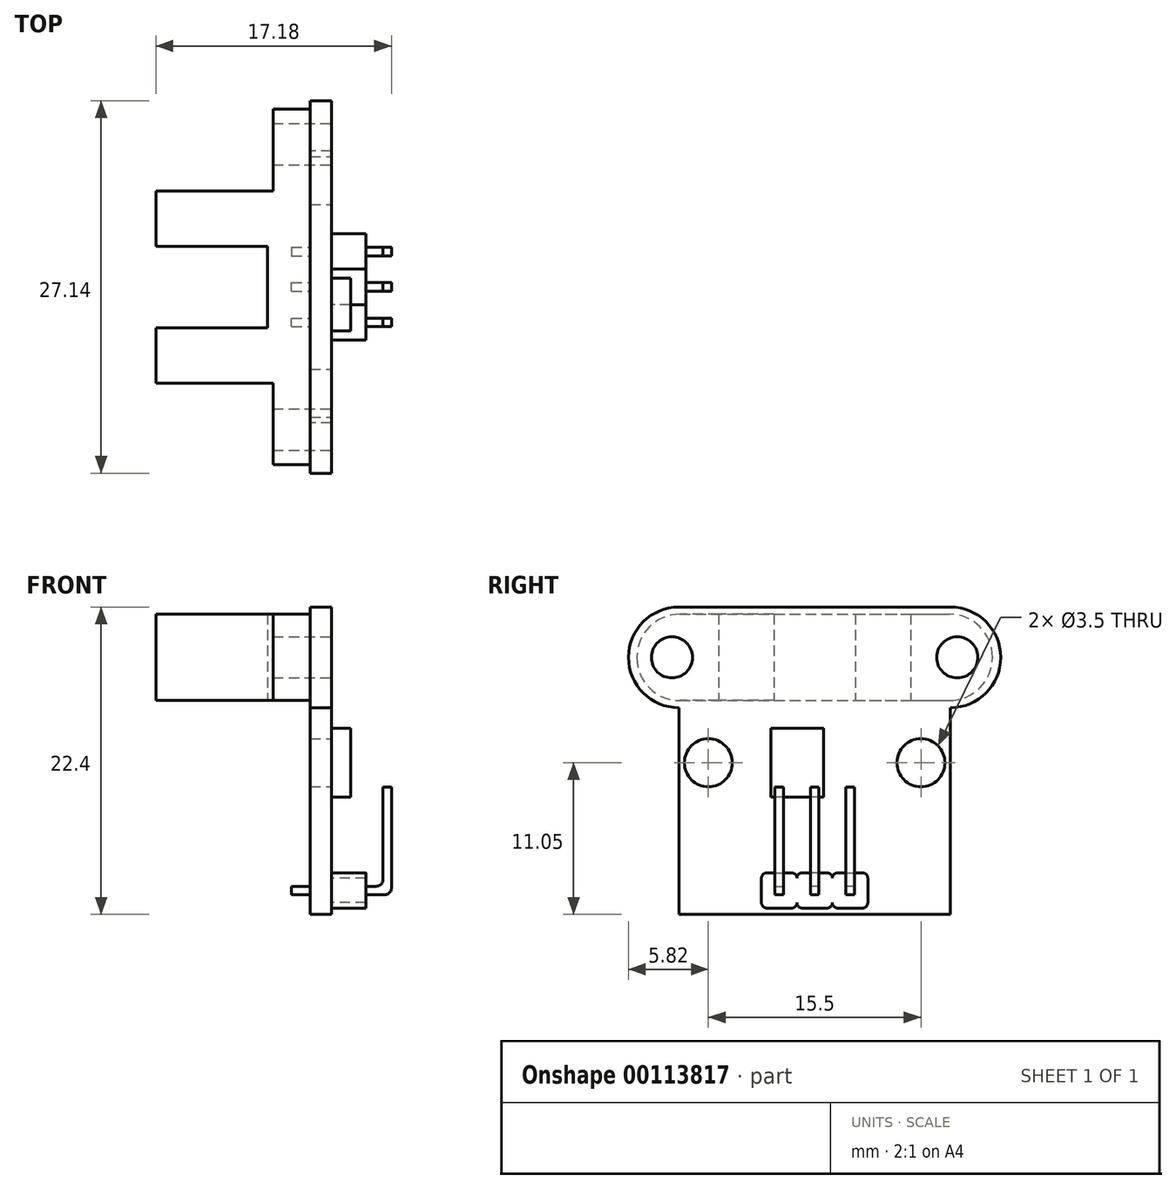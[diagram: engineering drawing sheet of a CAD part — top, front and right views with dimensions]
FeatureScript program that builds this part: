
annotation { "Feature Type Name" : "Feature", "Feature Type Description" : "" }
export const myFeature = defineFeature(function(context is Context, id is Id, definition is map)
    precondition{}
    {
        {
            var Q0;
            Q0=qCreatedBy(makeId("Top.planeOp"),FACE);
            var sketch = newSketch(context, id + "F0", { "sketchPlane" : qUnion([Q0])});
            skLineSegment(sketch, "E0", {"start": v(0, 0) * mm, "end": v(83.87, 0) * mm, "construction": true});
            skLineSegment(sketch, "E1", {"start": v(0, 0) * mm, "end": v(0, -2.97) * mm});
            skLineSegment(sketch, "E2", {"start": v(0, -2.97) * mm, "end": v(-8.13, -2.97) * mm});
            skLineSegment(sketch, "E3", {"start": v(-8.13, -2.97) * mm, "end": v(-8.13, -7) * mm});
            skLineSegment(sketch, "E4", {"start": v(-8.13, -7) * mm, "end": v(0.41, -7) * mm});
            skLineSegment(sketch, "E5", {"start": v(0.41, -7) * mm, "end": v(0.41, -12.97) * mm});
            skLineSegment(sketch, "E6", {"start": v(0.41, -12.96) * mm, "end": v(3.13, -12.96) * mm});
            skLineSegment(sketch, "E7", {"start": v(3.13, -12.96) * mm, "end": v(3.13, 0) * mm});
            skLineSegment(sketch, "E8.MirrorCS", {"start": v(0.41, 7) * mm, "end": v(0.41, 12.97) * mm});
            skLineSegment(sketch, "E9.MirrorCS", {"start": v(0.4, 12.97) * mm, "end": v(3.13, 12.97) * mm});
            skLineSegment(sketch, "E10.MirrorCS", {"start": v(0, 0) * mm, "end": v(0, 2.97) * mm});
            skLineSegment(sketch, "E11.MirrorCS", {"start": v(3.13, 12.96) * mm, "end": v(3.13, 0) * mm});
            skLineSegment(sketch, "E12.MirrorCS", {"start": v(0, 2.97) * mm, "end": v(-8.13, 2.97) * mm});
            skLineSegment(sketch, "E13.MirrorCS", {"start": v(-8.13, 7) * mm, "end": v(0.41, 7) * mm});
            skLineSegment(sketch, "E14.MirrorCS", {"start": v(-8.13, 2.97) * mm, "end": v(-8.13, 7) * mm});
            skLineSegment(sketch, "E15", {"start": v(-8.13, -2.97) * mm, "end": v(-8.13, 2.97) * mm, "construction": true});
            skSolve(sketch);
        }
        {
            var Q0;
            Q0=qSketchRegion(id+"F0",true);
            extrude(context, id + "F1", {"entities" : qUnion([Q0]), "endBound" : BoundingType.SYMMETRIC, "depth" : 6.3 * mm});
        }
        {
            var Q0;
            Q0=makeQuery(id+"F1.opExtrude","CAP_EDGE",EDGE,{"disambiguationData":[OSD([sQuery(id+"F0.wireOp",EDGE,"E9.MirrorCS")])],"isStart":false});
            var Q1;
            Q1=makeQuery(id+"F1.opExtrude","CAP_EDGE",EDGE,{"disambiguationData":[OSD([sQuery(id+"F0.wireOp",EDGE,"E9.MirrorCS")])],"isStart":true});
            var Q2;
            Q2=makeQuery(id+"F1.opExtrude","CAP_EDGE",EDGE,{"disambiguationData":[OSD([sQuery(id+"F0.wireOp",EDGE,"E6")])],"isStart":false});
            var Q3;
            Q3=makeQuery(id+"F1.opExtrude","CAP_EDGE",EDGE,{"disambiguationData":[OSD([sQuery(id+"F0.wireOp",EDGE,"E6")])],"isStart":true});
            fillet(context, id + "F2", {"entities" : qUnion([Q0, Q1, Q2, Q3]), "radius" : 3.14 * mm, "tangentPropagation" : true, "allowEdgeOverflow" : false});
        }
        {
            var Q0;
            Q0=makeQuery(id+"F1.opExtrude","SWEPT_FACE",FACE,{"disambiguationData":[OSD([sQuery(id+"F0.wireOp",EDGE,"E7"),sQuery(id+"F0.wireOp",EDGE,"E11.MirrorCS")])]});
            var sketch = newSketch(context, id + "F3", { "sketchPlane" : qUnion([Q0])});
            skLineSegment(sketch, "E16", {"start": v(0, 3.15) * mm, "end": v(0, -3.15) * mm, "construction": true});
            skLineSegment(sketch, "E17", {"start": v(-9.9, -18.73) * mm, "end": v(-9.9, -3.67) * mm});
            skArc(sketch, "E18", {"start": v(-9.9, 3.67) * mm, "mid": v(-13.57, 0) * mm, "end": v(-9.9, -3.67) * mm});
            skLineSegment(sketch, "E19.MirrorCS", {"start": v(9.9, -18.73) * mm, "end": v(9.9, -3.67) * mm});
            skArc(sketch, "E20.MirrorCS", {"start": v(9.9, 3.67) * mm, "mid": v(13.57, 0) * mm, "end": v(9.9, -3.67) * mm});
            skLineSegment(sketch, "E21", {"start": v(9.9, 3.67) * mm, "end": v(-9.9, 3.67) * mm});
            skLineSegment(sketch, "E22", {"start": v(9.9, -18.73) * mm, "end": v(-9.9, -18.73) * mm});
            skCircle(sketch, "E23", {"center": v(-9.9, 0) * mm, "radius": 3.67 * mm});
            skCircle(sketch, "E24", {"center": v(9.9, 0) * mm, "radius": 3.67 * mm});
            skSolve(sketch);
        }
        {
            var Q0;
            Q0=makeQuery(id+"F1.opExtrude","SWEPT_FACE",FACE,{"disambiguationData":[OSD([sQuery(id+"F0.wireOp",EDGE,"E7"),sQuery(id+"F0.wireOp",EDGE,"E11.MirrorCS")])]});
            var sketch = newSketch(context, id + "F4", { "sketchPlane" : qUnion([Q0])});
            skLineSegment(sketch, "E25", {"start": v(-9.9, 0) * mm, "end": v(9.9, 0) * mm, "construction": true});
            skCircle(sketch, "E26", {"center": v(-10.4, 0) * mm, "radius": 1.5 * mm});
            skCircle(sketch, "E27.MirrorC", {"center": v(10.4, 0) * mm, "radius": 1.5 * mm});
            skCircle(sketch, "E28", {"center": v(-7.75, -7.68) * mm, "radius": 1.75 * mm});
            skCircle(sketch, "E29.MirrorC", {"center": v(7.75, -7.68) * mm, "radius": 1.75 * mm});
            skSolve(sketch);
        }
        {
            var Q0;
            Q0=qSketchRegion(id+"F3",true);
            extrude(context, id + "F5", {"entities" : qUnion([Q0]), "operationType" : NewBodyOperationType.ADD, "depth" : 1.54 * mm});
        }
        {
            var Q0;
            Q0=qSketchRegion(id+"F4",true);
            extrude(context, id + "F6", {"entities" : qUnion([Q0]), "operationType" : NewBodyOperationType.REMOVE, "endBound" : BoundingType.SYMMETRIC, "oppositeDirection" : true, "depth" : 25 * mm});
        }
        {
            var Q0;
            Q0=makeQuery(id+"F5.opExtrude","CAP_FACE",FACE,{"disambiguationData":[OSD([sQuery(id+"F3.wireOp",EDGE,"E17"),sQuery(id+"F3.wireOp",EDGE,"E18"),sQuery(id+"F3.wireOp",EDGE,"E19.MirrorCS"),sQuery(id+"F3.wireOp",EDGE,"E20.MirrorCS"),sQuery(id+"F3.wireOp",EDGE,"E21"),sQuery(id+"F3.wireOp",EDGE,"E22")])],"isStart":false});
            var sketch = newSketch(context, id + "F7", { "sketchPlane" : qUnion([Q0])});
            skLineSegment(sketch, "E30.bottom", {"start": v(0.9, -15.7) * mm, "end": v(-0.9, -15.7) * mm});
            skLineSegment(sketch, "E30.top", {"start": v(0.9, -18.28) * mm, "end": v(-0.9, -18.28) * mm});
            skLineSegment(sketch, "E30.left", {"start": v(1.3, -16.1) * mm, "end": v(1.3, -17.88) * mm});
            skLineSegment(sketch, "E30.right", {"start": v(-1.3, -16.1) * mm, "end": v(-1.3, -17.88) * mm});
            skPoint(sketch, "E30.middle", {"position": v(0, -16.99) * mm});
            skPoint(sketch, "E31.visualSharp", {"position": v(1.3, -15.7) * mm});
            skArc(sketch, "E31.filletArc", {"start": v(1.3, -16.1) * mm, "mid": v(1.17, -15.81) * mm, "end": v(0.9, -15.7) * mm});
            skPoint(sketch, "E32.visualSharp", {"position": v(1.3, -18.28) * mm});
            skArc(sketch, "E32.filletArc", {"start": v(0.9, -18.28) * mm, "mid": v(1.17, -18.16) * mm, "end": v(1.3, -17.88) * mm});
            skPoint(sketch, "E33.visualSharp", {"position": v(-1.3, -18.28) * mm});
            skArc(sketch, "E33.filletArc", {"start": v(-1.3, -17.88) * mm, "mid": v(-1.17, -18.16) * mm, "end": v(-0.9, -18.28) * mm});
            skPoint(sketch, "E34.visualSharp", {"position": v(-1.3, -15.7) * mm});
            skArc(sketch, "E34.filletArc", {"start": v(-0.9, -15.7) * mm, "mid": v(-1.17, -15.81) * mm, "end": v(-1.3, -16.1) * mm});
            skArc(sketch, "E35.MirrorCS", {"start": v(1.3, -16.1) * mm, "mid": v(1.4, -15.81) * mm, "end": v(1.7, -15.7) * mm});
            skArc(sketch, "E36.MirrorCS", {"start": v(3.47, -15.7) * mm, "mid": v(3.76, -15.81) * mm, "end": v(3.88, -16.1) * mm});
            skArc(sketch, "E37.MirrorCS", {"start": v(3.88, -17.88) * mm, "mid": v(3.76, -18.16) * mm, "end": v(3.47, -18.28) * mm});
            skArc(sketch, "E38.MirrorCS", {"start": v(1.7, -18.28) * mm, "mid": v(1.4, -18.16) * mm, "end": v(1.3, -17.88) * mm});
            skPoint(sketch, "E39.MirrorP", {"position": v(3.88, -15.7) * mm});
            skPoint(sketch, "E40.MirrorP", {"position": v(2.58, -16.99) * mm});
            skLineSegment(sketch, "E41.MirrorCS", {"start": v(3.88, -16.1) * mm, "end": v(3.88, -17.88) * mm});
            skLineSegment(sketch, "E42.MirrorCS", {"start": v(1.7, -15.7) * mm, "end": v(3.47, -15.7) * mm});
            skLineSegment(sketch, "E43.MirrorCS", {"start": v(1.7, -18.28) * mm, "end": v(3.47, -18.28) * mm});
            skPoint(sketch, "E44.MirrorP", {"position": v(3.88, -18.28) * mm});
            skArc(sketch, "E45.MirrorCS", {"start": v(-1.7, -15.7) * mm, "mid": v(-1.4, -15.81) * mm, "end": v(-1.3, -16.1) * mm});
            skPoint(sketch, "E46.MirrorP", {"position": v(-3.87, -15.7) * mm});
            skPoint(sketch, "E47.MirrorP", {"position": v(-3.87, -18.28) * mm});
            skArc(sketch, "E48.MirrorCS", {"start": v(-1.3, -17.88) * mm, "mid": v(-1.4, -18.16) * mm, "end": v(-1.7, -18.28) * mm});
            skPoint(sketch, "E49.MirrorP", {"position": v(-2.58, -16.99) * mm});
            skLineSegment(sketch, "E50.MirrorCS", {"start": v(-3.47, -15.7) * mm, "end": v(-1.7, -15.7) * mm});
            skLineSegment(sketch, "E51.MirrorCS", {"start": v(-3.47, -18.28) * mm, "end": v(-1.7, -18.28) * mm});
            skArc(sketch, "E52.MirrorCS", {"start": v(-3.87, -16.1) * mm, "mid": v(-3.76, -15.81) * mm, "end": v(-3.47, -15.7) * mm});
            skLineSegment(sketch, "E53.MirrorCS", {"start": v(-3.87, -16.1) * mm, "end": v(-3.87, -17.88) * mm});
            skArc(sketch, "E54.MirrorCS", {"start": v(-3.47, -18.28) * mm, "mid": v(-3.76, -18.16) * mm, "end": v(-3.88, -17.88) * mm});
            skSolve(sketch);
        }
        {
            var Q0;
            Q0 = qSketchRegion(id + "F7", true);
            extrude(context, id + "F8", {"entities" : qUnion([Q0]), "operationType" : NewBodyOperationType.ADD, "depth" : 2.5 * mm});
        }
        {
            var Q0;
            Q0=makeQuery(id+"F8.opExtrude","CAP_FACE",FACE,{"disambiguationData":[OSD([sQuery(id+"F7.wireOp",EDGE,"E30.bottom"),sQuery(id+"F7.wireOp",EDGE,"E30.top"),sQuery(id+"F7.wireOp",EDGE,"E31.filletArc"),sQuery(id+"F7.wireOp",EDGE,"E32.filletArc"),sQuery(id+"F7.wireOp",EDGE,"E33.filletArc"),sQuery(id+"F7.wireOp",EDGE,"E34.filletArc"),sQuery(id+"F7.wireOp",EDGE,"E35.MirrorCS"),sQuery(id+"F7.wireOp",EDGE,"E36.MirrorCS"),sQuery(id+"F7.wireOp",EDGE,"E37.MirrorCS"),sQuery(id+"F7.wireOp",EDGE,"E38.MirrorCS"),sQuery(id+"F7.wireOp",EDGE,"E41.MirrorCS"),sQuery(id+"F7.wireOp",EDGE,"E42.MirrorCS"),sQuery(id+"F7.wireOp",EDGE,"E43.MirrorCS"),sQuery(id+"F7.wireOp",EDGE,"E45.MirrorCS"),sQuery(id+"F7.wireOp",EDGE,"E48.MirrorCS"),sQuery(id+"F7.wireOp",EDGE,"E50.MirrorCS"),sQuery(id+"F7.wireOp",EDGE,"E51.MirrorCS"),sQuery(id+"F7.wireOp",EDGE,"E52.MirrorCS"),sQuery(id+"F7.wireOp",EDGE,"E53.MirrorCS"),sQuery(id+"F7.wireOp",EDGE,"E54.MirrorCS")])],"isStart":false});
            var sketch = newSketch(context, id + "F9", { "sketchPlane" : qUnion([Q0])});
            skLineSegment(sketch, "E55", {"start": v(1.3, -16.1) * mm, "end": v(1.3, -17.88) * mm, "construction": true});
            skLineSegment(sketch, "E56", {"start": v(-1.3, -16.1) * mm, "end": v(-1.3, -17.88) * mm, "construction": true});
            skLineSegment(sketch, "E57.bottom", {"start": v(0.31, -16.68) * mm, "end": v(-0.3, -16.68) * mm});
            skLineSegment(sketch, "E57.top", {"start": v(0.31, -17.3) * mm, "end": v(-0.3, -17.3) * mm});
            skLineSegment(sketch, "E57.left", {"start": v(0.31, -16.68) * mm, "end": v(0.31, -17.3) * mm});
            skLineSegment(sketch, "E57.right", {"start": v(-0.3, -16.68) * mm, "end": v(-0.3, -17.3) * mm});
            skPoint(sketch, "E57.middle", {"position": v(0, -16.99) * mm});
            skPoint(sketch, "E58", {"position": v(-1.3, -16.99) * mm});
            skLineSegment(sketch, "E59.MirrorCS", {"start": v(2.27, -16.68) * mm, "end": v(2.9, -16.68) * mm});
            skPoint(sketch, "E60.MirrorP", {"position": v(2.58, -16.99) * mm});
            skLineSegment(sketch, "E61.MirrorCS", {"start": v(2.27, -17.3) * mm, "end": v(2.9, -17.3) * mm});
            skLineSegment(sketch, "E62.MirrorCS", {"start": v(2.27, -16.68) * mm, "end": v(2.27, -17.3) * mm});
            skLineSegment(sketch, "E63.MirrorCS", {"start": v(2.9, -16.68) * mm, "end": v(2.9, -17.3) * mm});
            skPoint(sketch, "E64.MirrorP", {"position": v(-2.58, -16.99) * mm});
            skLineSegment(sketch, "E65.MirrorCS", {"start": v(-2.9, -16.68) * mm, "end": v(-2.9, -17.3) * mm});
            skLineSegment(sketch, "E66.MirrorCS", {"start": v(-2.27, -16.68) * mm, "end": v(-2.27, -17.3) * mm});
            skLineSegment(sketch, "E67.MirrorCS", {"start": v(-2.9, -17.3) * mm, "end": v(-2.27, -17.3) * mm});
            skLineSegment(sketch, "E68.MirrorCS", {"start": v(-2.9, -16.68) * mm, "end": v(-2.27, -16.68) * mm});
            skSolve(sketch);
        }
        {
            var Q0;
            Q0 = qSketchRegion(id + "F9", true);
            extrude(context, id + "F10", {"entities" : qUnion([Q0]), "operationType" : NewBodyOperationType.ADD, "depth" : 1.88 * mm});
        }
        {
            var Q0;
            Q0=makeQuery(id+"F3.imprint","IMPRINT",FACE,{"disambiguationData":[TD([[makeQuery(id+"F3.imprint","IMPRINT",EDGE,{"derivedFrom":sQuery(id+"F3.wireOp",EDGE,"E17")}),-1.0]])]});
            var sketch = newSketch(context, id + "F11", { "sketchPlane" : qUnion([Q0])});
            skLineSegment(sketch, "E69.0", {"start": v(-2.9, -16.68) * mm, "end": v(-2.27, -16.68) * mm});
            skLineSegment(sketch, "E70.0.0", {"start": v(-2.27, -16.68) * mm, "end": v(-2.9, -16.68) * mm});
            skLineSegment(sketch, "E70.0.1", {"start": v(-2.9, -16.68) * mm, "end": v(-2.9, -17.3) * mm});
            skLineSegment(sketch, "E70.0.2", {"start": v(-2.9, -17.3) * mm, "end": v(-2.27, -17.3) * mm});
            skLineSegment(sketch, "E70.0.3", {"start": v(-2.27, -17.3) * mm, "end": v(-2.27, -16.68) * mm});
            skLineSegment(sketch, "E71.0.0", {"start": v(0.31, -17.3) * mm, "end": v(0.31, -16.68) * mm});
            skLineSegment(sketch, "E71.0.1", {"start": v(0.31, -16.68) * mm, "end": v(-0.3, -16.68) * mm});
            skLineSegment(sketch, "E71.0.2", {"start": v(-0.3, -16.68) * mm, "end": v(-0.3, -17.3) * mm});
            skLineSegment(sketch, "E71.0.3", {"start": v(-0.3, -17.3) * mm, "end": v(0.31, -17.3) * mm});
            skLineSegment(sketch, "E72.0.0", {"start": v(2.9, -16.68) * mm, "end": v(2.27, -16.68) * mm});
            skLineSegment(sketch, "E72.0.1", {"start": v(2.27, -16.68) * mm, "end": v(2.27, -17.3) * mm});
            skLineSegment(sketch, "E72.0.2", {"start": v(2.27, -17.3) * mm, "end": v(2.9, -17.3) * mm});
            skLineSegment(sketch, "E72.0.3", {"start": v(2.9, -17.3) * mm, "end": v(2.9, -16.68) * mm});
            skSolve(sketch);
        }
        {
            var Q0;
            Q0 = qSketchRegion(id + "F11", true);
            extrude(context, id + "F12", {"entities" : qUnion([Q0]), "operationType" : NewBodyOperationType.ADD, "oppositeDirection" : true, "depth" : 1.36 * mm});
        }
        {
            var Q0;
            Q0=makeQuery(id+"F10.opExtrude","SWEPT_FACE",FACE,{"disambiguationData":[OSD([sQuery(id+"F9.wireOp",EDGE,"E67.MirrorCS")])]});
            var sketch = newSketch(context, id + "F13", { "sketchPlane" : qUnion([Q0])});
            skLineSegment(sketch, "E73.bottom", {"start": v(9.05, 2.9) * mm, "end": v(8.43, 2.9) * mm});
            skLineSegment(sketch, "E73.top", {"start": v(9.05, 2.27) * mm, "end": v(8.43, 2.27) * mm});
            skLineSegment(sketch, "E73.left", {"start": v(9.05, 2.9) * mm, "end": v(9.05, 2.27) * mm});
            skLineSegment(sketch, "E73.right", {"start": v(8.43, 2.9) * mm, "end": v(8.43, 2.27) * mm});
            skLineSegment(sketch, "E74.bottom", {"start": v(9.05, 0.3) * mm, "end": v(8.43, 0.3) * mm});
            skLineSegment(sketch, "E74.top", {"start": v(9.05, -0.31) * mm, "end": v(8.43, -0.31) * mm});
            skLineSegment(sketch, "E74.left", {"start": v(9.05, 0.3) * mm, "end": v(9.05, -0.31) * mm});
            skLineSegment(sketch, "E74.right", {"start": v(8.43, 0.3) * mm, "end": v(8.43, -0.31) * mm});
            skLineSegment(sketch, "E75.bottom", {"start": v(9.05, -2.27) * mm, "end": v(8.43, -2.27) * mm});
            skLineSegment(sketch, "E75.top", {"start": v(9.05, -2.9) * mm, "end": v(8.43, -2.9) * mm});
            skLineSegment(sketch, "E75.left", {"start": v(9.05, -2.27) * mm, "end": v(9.05, -2.9) * mm});
            skLineSegment(sketch, "E75.right", {"start": v(8.43, -2.27) * mm, "end": v(8.43, -2.9) * mm});
            skSolve(sketch);
        }
        {
            var Q0;
            Q0 = qSketchRegion(id + "F13", true);
            extrude(context, id + "F14", {"entities" : qUnion([Q0]), "operationType" : NewBodyOperationType.ADD, "oppositeDirection" : true, "depth" : 7.85 * mm});
        }
        {
            var Q0;
            Q0=makeQuery(id+"F10.opExtrude","CAP_EDGE",EDGE,{"disambiguationData":[OSD([sQuery(id+"F9.wireOp",EDGE,"E61.MirrorCS")])],"isStart":false});
            var Q1;
            Q1=makeQuery(id+"F10.opExtrude","CAP_EDGE",EDGE,{"disambiguationData":[OSD([sQuery(id+"F9.wireOp",EDGE,"E57.top")])],"isStart":false});
            var Q2;
            Q2=makeQuery(id+"F10.opExtrude","CAP_EDGE",EDGE,{"disambiguationData":[OSD([sQuery(id+"F9.wireOp",EDGE,"E67.MirrorCS")])],"isStart":false});
            var Q3;
            Q3=makeQuery(id+"F14.boolean.opBoolean","INTERSECT",EDGE,{"derivedFrom":[makeQuery(id+"F10.opExtrude","SWEPT_FACE",FACE,{"disambiguationData":[OSD([sQuery(id+"F9.wireOp",EDGE,"E59.MirrorCS")])]}),makeQuery(id+"F14.opExtrude","SWEPT_FACE",FACE,{"disambiguationData":[OSD([sQuery(id+"F13.wireOp",EDGE,"E75.right")])]})]});
            var Q4;
            Q4=makeQuery(id+"F14.boolean.opBoolean","INTERSECT",EDGE,{"derivedFrom":[makeQuery(id+"F10.opExtrude","SWEPT_FACE",FACE,{"disambiguationData":[OSD([sQuery(id+"F9.wireOp",EDGE,"E57.bottom")])]}),makeQuery(id+"F14.opExtrude","SWEPT_FACE",FACE,{"disambiguationData":[OSD([sQuery(id+"F13.wireOp",EDGE,"E74.right")])]})]});
            var Q5;
            Q5=makeQuery(id+"F14.boolean.opBoolean","INTERSECT",EDGE,{"derivedFrom":[makeQuery(id+"F10.opExtrude","SWEPT_FACE",FACE,{"disambiguationData":[OSD([sQuery(id+"F9.wireOp",EDGE,"E68.MirrorCS")])]}),makeQuery(id+"F14.opExtrude","SWEPT_FACE",FACE,{"disambiguationData":[OSD([sQuery(id+"F13.wireOp",EDGE,"E73.right")])]})]});
            fillet(context, id + "F15", {"entities" : qUnion([Q0, Q1, Q2, Q3, Q4, Q5]), "radius" : 0.5 * mm, "tangentPropagation" : true, "allowEdgeOverflow" : false});
        }
        {
            var Q0;
            Q0=makeQuery(id+"F5.opExtrude","CAP_FACE",FACE,{"disambiguationData":[OSD([sQuery(id+"F3.wireOp",EDGE,"E17"),sQuery(id+"F3.wireOp",EDGE,"E18"),sQuery(id+"F3.wireOp",EDGE,"E19.MirrorCS"),sQuery(id+"F3.wireOp",EDGE,"E20.MirrorCS"),sQuery(id+"F3.wireOp",EDGE,"E21"),sQuery(id+"F3.wireOp",EDGE,"E22")])],"isStart":false});
            var sketch = newSketch(context, id + "F16", { "sketchPlane" : qUnion([Q0])});
            skLineSegment(sketch, "E76", {"start": v(-7.75, -7.68) * mm, "end": v(7.75, -7.68) * mm, "construction": true});
            skLineSegment(sketch, "E77.bottom", {"start": v(0.65, -5.18) * mm, "end": v(-3.2, -5.18) * mm});
            skLineSegment(sketch, "E77.top", {"start": v(0.65, -10.18) * mm, "end": v(-3.2, -10.18) * mm});
            skLineSegment(sketch, "E77.left", {"start": v(0.65, -5.18) * mm, "end": v(0.65, -10.18) * mm});
            skLineSegment(sketch, "E77.right", {"start": v(-3.2, -5.18) * mm, "end": v(-3.2, -10.18) * mm});
            skPoint(sketch, "E77.middle", {"position": v(-1.27, -7.68) * mm});
            skSolve(sketch);
        }
        {
            var Q0;
            Q0 = qSketchRegion(id + "F16", true);
            extrude(context, id + "F17", {"entities" : qUnion([Q0]), "operationType" : NewBodyOperationType.ADD, "depth" : 1.4 * mm});
        }
        {
            var Q0;
            Q0=qCreatedBy(makeId("Front.planeOp"),FACE);
            var sketch = newSketch(context, id + "F18", { "sketchPlane" : qUnion([Q0])});
            skLineSegment(sketch, "E78", {"start": v(0, 0) * mm, "end": v(-14.38, 0) * mm, "construction": true});
            skLineSegment(sketch, "E79.0", {"start": v(-8.13, 3.15) * mm, "end": v(-8.13, -3.15) * mm, "construction": true});
            skPoint(sketch, "E80", {"position": v(-8.13, 0) * mm});
            skPoint(sketch, "E81", {"position": v(-4.98, 0) * mm});
            skLineSegment(sketch, "E82", {"start": v(-8.13, 0) * mm, "end": v(-4.98, 0) * mm});
            skLineSegment(sketch, "E83", {"start": v(-8.13, 3.15) * mm, "end": v(-8.13, 0) * mm, "construction": true});
            skSolve(sketch);
        }
    });
